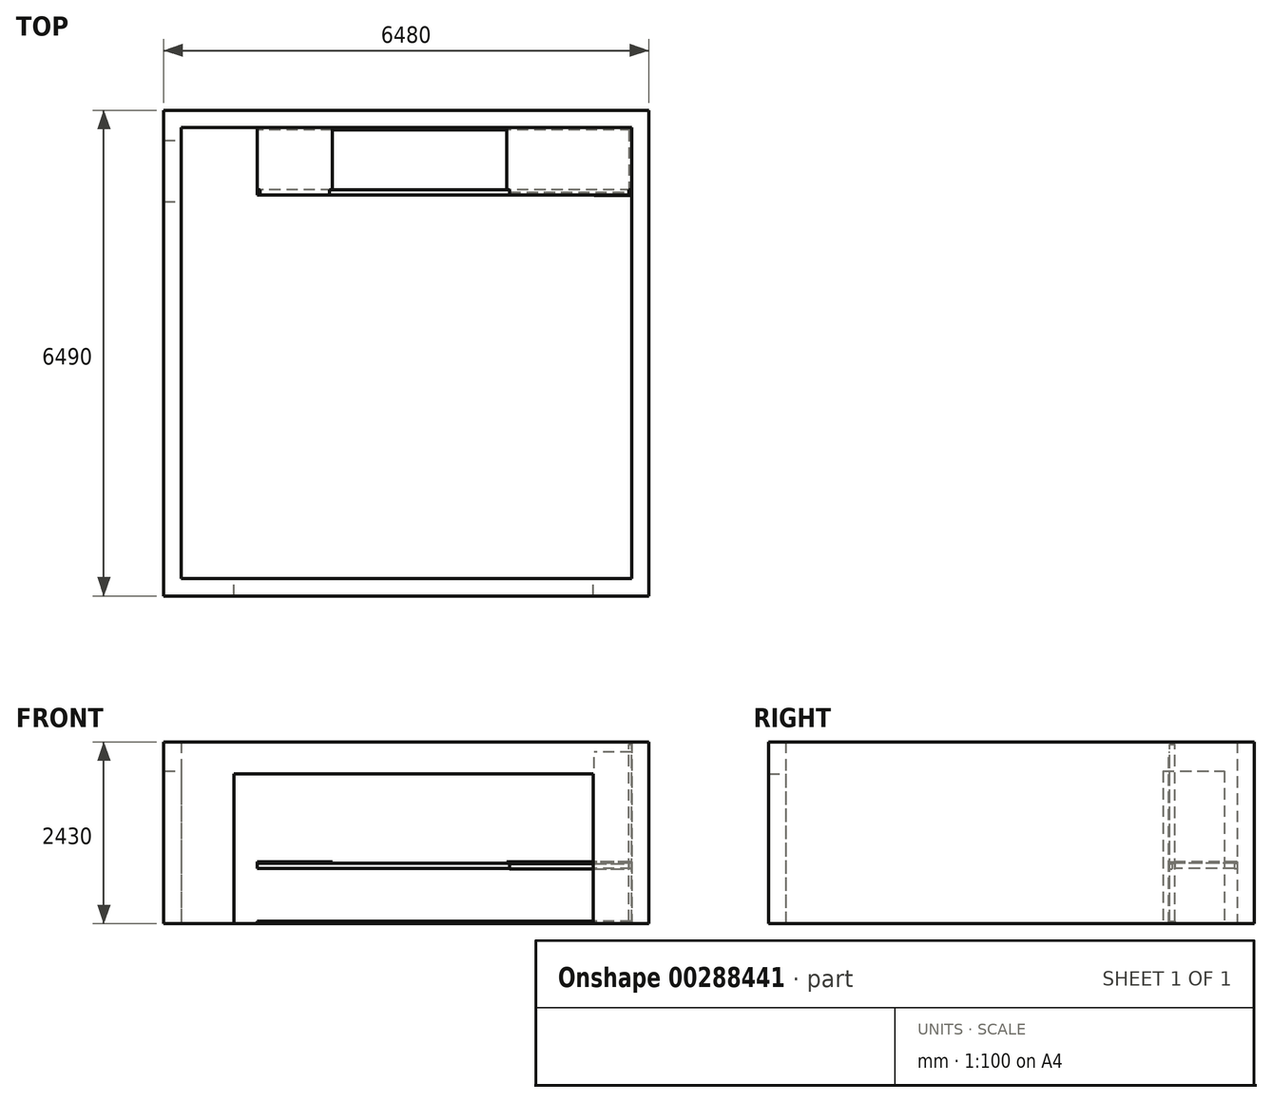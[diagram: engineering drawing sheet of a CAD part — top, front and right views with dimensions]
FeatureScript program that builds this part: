
annotation { "Feature Type Name" : "Feature", "Feature Type Description" : "" }
export const myFeature = defineFeature(function(context is Context, id is Id, definition is map)
    precondition{}
    {
        {
            var Q0;
            Q0=qCreatedBy(makeId("Top.planeOp"),FACE);
            var sketch = newSketch(context, id + "F0", { "sketchPlane" : qUnion([Q0])});
            skLineSegment(sketch, "E0.bottom", {"start": v(3010, -3015) * mm, "end": v(-3010, -3015) * mm});
            skLineSegment(sketch, "E0.top", {"start": v(3010, 3015) * mm, "end": v(-3010, 3015) * mm});
            skLineSegment(sketch, "E0.left", {"start": v(3010, -3015) * mm, "end": v(3010, 3015) * mm});
            skLineSegment(sketch, "E0.right", {"start": v(-3010, -3015) * mm, "end": v(-3010, 3015) * mm});
            skPoint(sketch, "E0.middle", {"position": v(0, 0) * mm});
            skLineSegment(sketch, "E1.0", {"start": v(-3240, -3245) * mm, "end": v(-3240, 3245) * mm});
            skLineSegment(sketch, "E1.1", {"start": v(3240, -3245) * mm, "end": v(-3240, -3245) * mm});
            skLineSegment(sketch, "E1.2", {"start": v(3240, -3245) * mm, "end": v(3240, 3245) * mm});
            skLineSegment(sketch, "E1.3", {"start": v(3240, 3245) * mm, "end": v(-3240, 3245) * mm});
            skSolve(sketch);
        }
        {
            var Q0;
            Q0 = qSketchRegion(id + "F0", true);
            extrude(context, id + "F1", {"entities" : qUnion([Q0]), "depth" : 2430 * mm});
        }
        {
            var Q0;
            Q0=qCreatedBy(makeId("Front.planeOp"),FACE);
            var sketch = newSketch(context, id + "F2", { "sketchPlane" : qUnion([Q0])});
            skLineSegment(sketch, "E2.bottom", {"start": v(-2300, 0) * mm, "end": v(2500, 0) * mm});
            skLineSegment(sketch, "E2.top", {"start": v(-2300, 2000) * mm, "end": v(2500, 2000) * mm});
            skLineSegment(sketch, "E2.left", {"start": v(-2300, 0) * mm, "end": v(-2300, 2000) * mm});
            skLineSegment(sketch, "E2.right", {"start": v(2500, 0) * mm, "end": v(2500, 2000) * mm});
            skSolve(sketch);
        }
        {
            var Q0;
            Q0 = qSketchRegion(id + "F2", true);
            extrude(context, id + "F3", {"entities" : qUnion([Q0]), "operationType" : NewBodyOperationType.REMOVE, "endBound" : BoundingType.THROUGH_ALL, "depth" : 25 * mm});
        }
        {
            var Q0;
            Q0=qCreatedBy(makeId("Right.planeOp"),FACE);
            var sketch = newSketch(context, id + "F4", { "sketchPlane" : qUnion([Q0])});
            skLineSegment(sketch, "E3.bottom", {"start": v(2845, 0) * mm, "end": v(2025, 0) * mm});
            skLineSegment(sketch, "E3.top", {"start": v(2845, 2040) * mm, "end": v(2025, 2040) * mm});
            skLineSegment(sketch, "E3.left", {"start": v(2845, 0) * mm, "end": v(2845, 2040) * mm});
            skLineSegment(sketch, "E3.right", {"start": v(2025, 0) * mm, "end": v(2025, 2040) * mm});
            skSolve(sketch);
        }
        {
            var Q0;
            Q0 = qSketchRegion(id + "F4", true);
            extrude(context, id + "F5", {"entities" : qUnion([Q0]), "operationType" : NewBodyOperationType.REMOVE, "endBound" : BoundingType.THROUGH_ALL, "oppositeDirection" : true, "depth" : 25 * mm});
        }
        {
            var Q0;
            Q0=makeQuery(id+"F1.opExtrude","SWEPT_FACE",FACE,{"disambiguationData":[OSD([sQuery(id+"F0.wireOp",EDGE,"E0.top")])]});
            var sketch = newSketch(context, id + "F6", { "sketchPlane" : qUnion([Q0])});
            skLineSegment(sketch, "E4.bottom", {"start": v(3010, 740) * mm, "end": v(-1990, 740) * mm});
            skLineSegment(sketch, "E4.top", {"start": v(3010, 810) * mm, "end": v(-1990, 810) * mm});
            skLineSegment(sketch, "E4.left", {"start": v(3010, 740) * mm, "end": v(3010, 810) * mm});
            skLineSegment(sketch, "E4.right", {"start": v(-1990, 740) * mm, "end": v(-1990, 810) * mm});
            skSolve(sketch);
        }
        {
            var Q0;
            Q0=makeQuery(id+"F6.imprint","IMPRINT",FACE,{"disambiguationData":[TD([[makeQuery(id+"F6.imprint","IMPRINT",EDGE,{"derivedFrom":sQuery(id+"F6.wireOp",EDGE,"E4.bottom")}),-1.0]])]});
            extrude(context, id + "F7", {"entities" : qUnion([Q0]), "offsetDistance" : 25 * mm, "depth" : 35 * mm});
        }
        {
            var Q0;
            Q0=makeQuery(id+"F1.opExtrude","SWEPT_FACE",FACE,{"disambiguationData":[OSD([sQuery(id+"F0.wireOp",EDGE,"E0.left")])]});
            var sketch = newSketch(context, id + "F8", { "sketchPlane" : qUnion([Q0])});
            skLineSegment(sketch, "E5.bottom", {"start": v(-2980, 810) * mm, "end": v(-2185, 810) * mm});
            skLineSegment(sketch, "E5.top", {"start": v(-2980, 740) * mm, "end": v(-2185, 740) * mm});
            skLineSegment(sketch, "E5.left", {"start": v(-2980, 810) * mm, "end": v(-2980, 740) * mm});
            skLineSegment(sketch, "E5.right", {"start": v(-2185, 810) * mm, "end": v(-2185, 740) * mm});
            skSolve(sketch);
        }
        {
            var Q0;
            Q0 = qSketchRegion(id + "F8", true);
            extrude(context, id + "F9", {"entities" : qUnion([Q0]), "offsetDistance" : 25 * mm, "depth" : 35 * mm});
        }
        {
            var Q0;
            Q0=makeQuery(id+"F1.opExtrude","SWEPT_FACE",FACE,{"disambiguationData":[OSD([sQuery(id+"F0.wireOp",EDGE,"E0.left")])]});
            var sketch = newSketch(context, id + "F10", { "sketchPlane" : qUnion([Q0])});
            skLineSegment(sketch, "E6.bottom", {"start": v(-2115, 35) * mm, "end": v(-2185, 35) * mm});
            skLineSegment(sketch, "E6.top", {"start": v(-2115, 2395) * mm, "end": v(-2185, 2395) * mm});
            skLineSegment(sketch, "E6.left", {"start": v(-2115, 35) * mm, "end": v(-2115, 2395) * mm});
            skLineSegment(sketch, "E6.right", {"start": v(-2185, 35) * mm, "end": v(-2185, 2395) * mm});
            skSolve(sketch);
        }
        {
            var Q0;
            Q0 = qSketchRegion(id + "F10", true);
            extrude(context, id + "F11", {"entities" : qUnion([Q0]), "offsetDistance" : 25 * mm, "depth" : 35 * mm});
        }
        {
            var Q0;
            Q0=qCreatedBy(makeId("Top.planeOp"),FACE);
            var sketch = newSketch(context, id + "F12", { "sketchPlane" : qUnion([Q0])});
            skLineSegment(sketch, "E7.bottom", {"start": v(3010, 2185) * mm, "end": v(-1990, 2185) * mm});
            skLineSegment(sketch, "E7.top", {"start": v(3010, 2115) * mm, "end": v(-1990, 2115) * mm});
            skLineSegment(sketch, "E7.right", {"start": v(-1990, 2185) * mm, "end": v(-1990, 2115) * mm});
            skLineSegment(sketch, "E8", {"start": v(3010, 2185) * mm, "end": v(3010, 2115) * mm});
            skSolve(sketch);
        }
        {
            var Q0;
            Q0 = qSketchRegion(id + "F12", true);
            extrude(context, id + "F13", {"entities" : qUnion([Q0]), "offsetDistance" : 25 * mm, "depth" : 35 * mm});
        }
        {
            var Q0;
            Q0=makeQuery(id+"F11.opExtrude","SWEPT_FACE",FACE,{"disambiguationData":[OSD([sQuery(id+"F10.wireOp",EDGE,"E6.left")])]});
            var sketch = newSketch(context, id + "F14", { "sketchPlane" : qUnion([Q0])});
            skLineSegment(sketch, "E9.bottom", {"start": v(3010, 6) * mm, "end": v(2510, 6) * mm});
            skLineSegment(sketch, "E9.top", {"start": v(3010, 2296) * mm, "end": v(2510, 2296) * mm});
            skLineSegment(sketch, "E9.left", {"start": v(3010, 6) * mm, "end": v(3010, 2296) * mm});
            skLineSegment(sketch, "E9.right", {"start": v(2510, 6) * mm, "end": v(2510, 2296) * mm});
            skSolve(sketch);
        }
        {
            var Q0;
            Q0 = qSketchRegion(id + "F14", true);
            extrude(context, id + "F15", {"entities" : qUnion([Q0]), "depth" : 10 * mm});
        }
        {
            var Q0;
            Q0=makeQuery(id+"F7.opExtrude","SWEPT_FACE",FACE,{"disambiguationData":[OSD([sQuery(id+"F6.wireOp",EDGE,"E4.top")])]});
            var sketch = newSketch(context, id + "F16", { "sketchPlane" : qUnion([Q0])});
            skLineSegment(sketch, "E10.bottom", {"start": v(3010, 3015) * mm, "end": v(1343.3, 3015) * mm});
            skLineSegment(sketch, "E11", {"start": v(3010, 3015) * mm, "end": v(3010, 2185) * mm});
            skLineSegment(sketch, "E12", {"start": v(3010, 2185) * mm, "end": v(2975, 2185) * mm});
            skLineSegment(sketch, "E13", {"start": v(2975, 2185) * mm, "end": v(2975, 2115) * mm});
            skLineSegment(sketch, "E14", {"start": v(1378.3, 2115) * mm, "end": v(1378.3, 2185) * mm});
            skLineSegment(sketch, "E15", {"start": v(1378.3, 2185) * mm, "end": v(1343.3, 2185) * mm});
            skLineSegment(sketch, "E16", {"start": v(1343.3, 2185) * mm, "end": v(1343.3, 3015) * mm});
            skLineSegment(sketch, "E17", {"start": v(2975, 2115) * mm, "end": v(1378.3, 2115) * mm});
            skSolve(sketch);
        }
        {
            var Q0;
            Q0 = qSketchRegion(id + "F16", true);
            extrude(context, id + "F17", {"entities" : qUnion([Q0]), "depth" : 16 * mm});
        }
        {
            var Q0;
            Q0=makeQuery(id+"F7.opExtrude","SWEPT_FACE",FACE,{"disambiguationData":[OSD([sQuery(id+"F6.wireOp",EDGE,"E4.top")])]});
            var sketch = newSketch(context, id + "F18", { "sketchPlane" : qUnion([Q0])});
            skLineSegment(sketch, "E18", {"start": v(-1990, 3015) * mm, "end": v(-990, 3015) * mm});
            skLineSegment(sketch, "E19", {"start": v(-990, 3015) * mm, "end": v(-990, 2185) * mm});
            skLineSegment(sketch, "E20", {"start": v(-990, 2185) * mm, "end": v(-1025, 2185) * mm});
            skLineSegment(sketch, "E21", {"start": v(-1025, 2185) * mm, "end": v(-1025, 2115) * mm});
            skLineSegment(sketch, "E22", {"start": v(-1025, 2115) * mm, "end": v(-1955, 2115) * mm});
            skLineSegment(sketch, "E23", {"start": v(-1955, 2115) * mm, "end": v(-1955, 2185) * mm});
            skLineSegment(sketch, "E24", {"start": v(-1955, 2185) * mm, "end": v(-1990, 2185) * mm});
            skLineSegment(sketch, "E25", {"start": v(-1990, 2185) * mm, "end": v(-1990, 3015) * mm});
            skSolve(sketch);
        }
        {
            var Q0;
            Q0 = qSketchRegion(id + "F18", true);
            extrude(context, id + "F19", {"entities" : qUnion([Q0]), "depth" : 16 * mm});
        }
        {
            var Q0;
            Q0=makeQuery(id+"F11.opExtrude","CAP_FACE",FACE,{"disambiguationData":[OSD([sQuery(id+"F10.wireOp",EDGE,"E6.bottom"),sQuery(id+"F10.wireOp",EDGE,"E6.top"),sQuery(id+"F10.wireOp",EDGE,"E6.left"),sQuery(id+"F10.wireOp",EDGE,"E6.right")])],"isStart":false});
            var sketch = newSketch(context, id + "F20", { "sketchPlane" : qUnion([Q0])});
            skLineSegment(sketch, "E26.bottom", {"start": v(-2115, 803.25) * mm, "end": v(-2150, 803.25) * mm});
            skLineSegment(sketch, "E26.top", {"start": v(-2115, 733.25) * mm, "end": v(-2150, 733.25) * mm});
            skLineSegment(sketch, "E26.left", {"start": v(-2115, 803.25) * mm, "end": v(-2115, 733.25) * mm});
            skLineSegment(sketch, "E26.right", {"start": v(-2150, 803.25) * mm, "end": v(-2150, 733.25) * mm});
            skSolve(sketch);
        }
        {
            var Q0;
            Q0 = qSketchRegion(id + "F20", true);
            extrude(context, id + "F21", {"entities" : qUnion([Q0]), "depth" : 1596.7 * mm, "offsetDistance" : 25 * mm});
        }
    });
